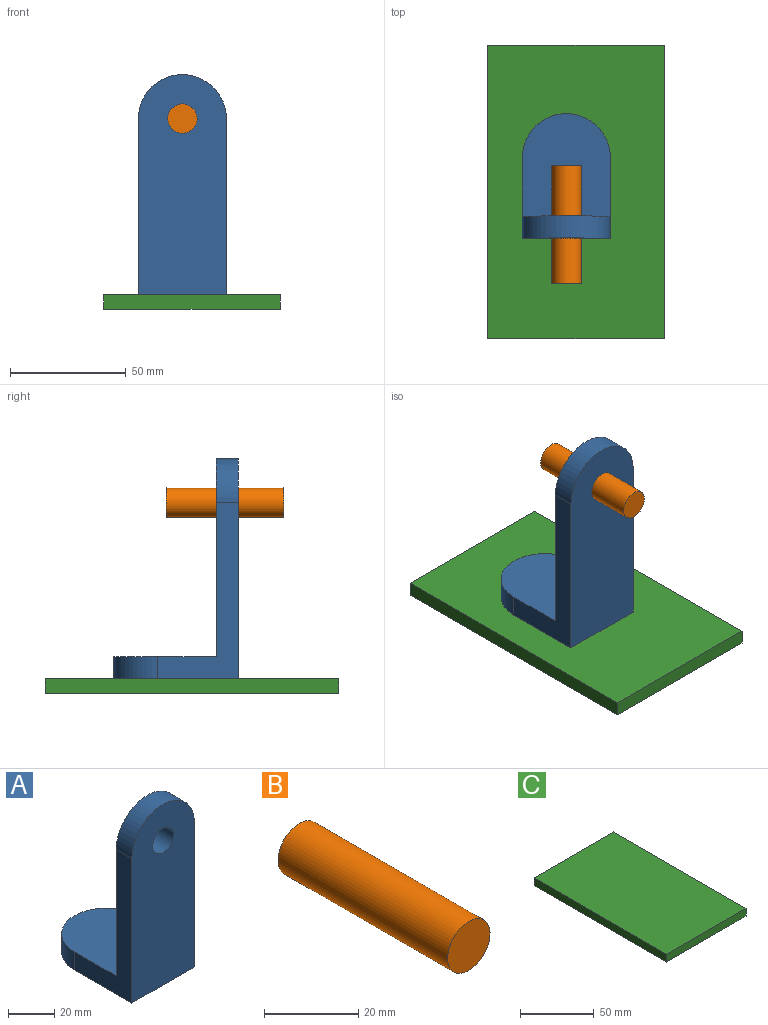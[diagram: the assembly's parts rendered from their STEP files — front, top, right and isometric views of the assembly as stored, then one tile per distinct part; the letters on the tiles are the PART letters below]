
ASSEMBLY  parts=3 mates=2
PART A: 9 faces, bbox 38.1x54x95.3 mm
  f0: plane 76.2x34.93mm, normal (-1,0,0), area 967.7mm2, adj f2,f3,f4,f5,f7,f8
  f1: plane 76.2x34.93mm, normal (1,0,0), area 967.7mm2, adj f2,f3,f4,f5,f7,f8
  f2: cylinder r=19.05mm len=38.1mm, axis (0,0,-1), area 570mm2, adj f0,f1,f3,f4
  f3: plane 44.45x38.1mm, normal (0,0,1), area 1537.8mm2, adj f0,f1,f2,f8
  f4: plane 53.98x38.1mm, normal (0,0,-1), area 1900.7mm2, adj f0,f1,f2,f7
  f5: cylinder r=19.05mm len=38.1mm, axis (0,1,0), area 570mm2, adj f0,f1,f7,f8
  f6: cylinder r=6.35mm len=12.7mm, axis (0,1,0), area 380mm2, adj f7,f8
  f7: plane 95.25x38.1mm, normal (0,-1,0), area 3346.6mm2, adj f0,f1,f4,f5,f6
  f8: plane 85.73x38.1mm, normal (0,1,0), area 2983.7mm2, adj f0,f1,f3,f5,f6
PART B: 3 faces, bbox 12.7x50.8x12.7 mm
  f0: cylinder r=6.35mm len=50.8mm, axis (0,1,0), area 2026.8mm2, adj f1,f2
  f1: plane 12.7x12.7mm, normal (0,-1,0), area 126.7mm2, adj f0
  f2: plane 12.7x12.7mm, normal (0,1,0), area 126.7mm2, adj f0
PART C: 6 faces, bbox 76.2x127x6.4 mm
  f0: plane 127x6.35mm, normal (-1,0,0), area 806.5mm2, adj f1,f3,f4,f5
  f1: plane 76.2x6.35mm, normal (0,-1,0), area 483.9mm2, adj f0,f2,f4,f5
  f2: plane 127x6.35mm, normal (1,0,0), area 806.5mm2, adj f1,f3,f4,f5
  f3: plane 76.2x6.35mm, normal (0,1,0), area 483.9mm2, adj f0,f2,f4,f5
  f4: plane 127x76.2mm, normal (0,0,1), area 9677.4mm2, adj f0,f1,f2,f3
  f5: plane 127x76.2mm, normal (0,0,-1), area 9677.4mm2, adj f0,f1,f2,f3
PLACE A t=(1.31,-30.36,-6.87)mm
PLACE B t=(20.36,-8.67,69.33)mm
PLACE C t=(-13.59,-83.31,-13.22)mm
MATE planar C.f4 <-> A.f4  axis (0,0,1) through (24.51,-19.81,-6.87)mm
MATE cylindrical B.f0 <-> A.f5  axis (0,1,0) through (20.36,-34.07,69.33)mm
